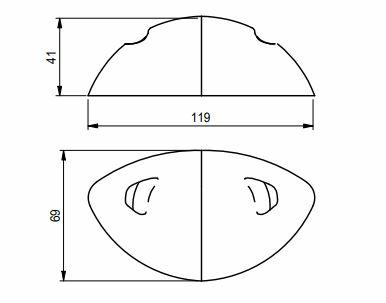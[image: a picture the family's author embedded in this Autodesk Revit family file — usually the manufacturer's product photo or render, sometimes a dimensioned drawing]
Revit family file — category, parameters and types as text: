
# Revit family: R-MBD-477
name_source: partatom
category: Portes
units: mm (PartAtom-declared; Revit-internal decimal feet)

## family parameters
Couper avec des vides une fois chargée = Non
Hôte = Mur
Partagée = Non
Repère de localisation dans la pièce = Oui
Toujours verticalement = Oui

## types (1)
- MBD-477
    1 Vantail = Oui
    2 Vantaux = Non
    A.E.V = non
    Acoustique = non
    Anti-Effraction = non
    Certification = D.A.S. Mode 2 certifié NF
    Code_MAJ = 2303130305MBD477
    Coloris_Chants = BER
    Coloris_Dormant = Hêtre
    Coloris_Face_Cote_Oppose_Ouverture = Prépeint
    Coloris_Face_Cote_Ouverture = Prépeint
    Construction analytique = <Aucun>
    DAS = Oui
    DC Larg Feuillure = 12 mm  [stored 0.0393701 ft]
    DC Pivot Vantail = 60 mm  [stored 0.19685 ft]
    Description = Bloc-porte bois D.A.S. 1 vantail avec pivot linteau motorisé encastré, double action / va-et-vient, EI30, D.A.S. certifié NF, sur huisserie bois
    Définir les propriétés thermiques par = Type schématique
    Ep Profil Pose Tunnel = 118 mm
    Ep Strat Vantail = 1 mm  [stored 0.00328084 ft]
    Ep Vantail = 46 mm  [stored 0.150919 ft]
    Epaisseur_Rainure à brique = 8 mm  [stored 0.0262467 ft]
    Fabricant = MALERBA
    Fiche_Produit = MBD-477
    Fileur = Non
    Hauteur_Tableau = 2125 mm
    Hauteur_Vantaux_Souhaitée = 2040 mm  [stored 6.69291 ft]
    Jeu_1 = 0 mm  [stored 0 ft]
    Jeu_2 = 0 mm  [stored 0 ft]
    Jeu_Côté_Articulation_Vantail = 8 mm  [stored 0.0262467 ft]
    Jeu_Côté_Fermeture_Vantail = 8 mm  [stored 0.0262467 ft]
    Jeu_Haut = 3 mm  [stored 0.00984252 ft]
    Larg Profil = 58 mm  [stored 0.190289 ft]
    Larg Profil Avec Fileur = 20 mm  [stored 0.0656168 ft]
    Larg Profil Trav = 76 mm  [stored 0.249344 ft]
    Largeur = 0 mm  [stored 0 ft]
    Largeur_Vantail_Semi_Fixe_Souhaitée = 930 mm  [stored 3.05118 ft]
    Largeur_Vantail_Service_Souhaitée = 930 mm  [stored 3.05118 ft]
    Mat APD = Caoutchouc noir
    Mat Parclose = BER 2
    Mat Parclose Métal = Peinture Laquée PMT - Blanc Pur - RAL 9010
    Materiaux_Dominant = Bois
    Modèle = Va et vient
    Montant_VV = Oui
    Note d'identification = 1V EI30 DAS - LINTEAU MOTORISE - HUISSERIE BOIS
    Pivot linteau motorisé = Oui
    Profondeur_Rainure à brique = 5 mm  [stored 0.0164042 ft]
    Reference_Commerciale = 1V/DA LINTEAU OP
    Resistance_Feu = EI30
    Sans_Montants = Non
    Sens_Feu = Recto / Verso
    Thermique (W/m2.°K) = 0
    URL = https://www.malerba.fr
    X_Axe Pivot = 114 mm  [stored 0.374016 ft]
    X_DC seuil = 9 mm  [stored 0.0295276 ft]
    X_Inv_DC Larg Feuillure_1V Montant = 12 mm  [stored 0.0393701 ft]

note: [stored X ft] marks values corroborated as IEEE doubles in the binary element streams (Revit-internal decimal feet)

## geometry (parser evidence)
native form markers: Blend x14
no freeform markers — native parametric forms only
